# Revit family: Q-SYS NC-110
name_source: partatom
category: Communication Devices
revit_build: Autodesk Revit 2018 (Build: 20190510_1515(x64)
units: mm (PartAtom-declared; Revit-internal decimal feet)

## family parameters
Cut with Voids When Loaded = No
Host = Face
Maintain Annotation Orientation = No
Part Type = Normal
Room Calculation Point = No
Round Connector Dimension = Use Diameter
Shared = No

## types (4) — shared parameters
Camera Material = Dark Material
Camera Type = Q-SYS ePTZ with Max H FOV 110°
Current Draw = 0.021
Default Elevation = 1270 mm
Depth = 42 mm  [stored 0.137795 ft]
Description = Q-SYS Networked Fixed-Lens ePTZ Camera
Focal Length = 1.86mm
Height = 34 mm
Lens Type = Integrated, Fixed
Lens Zoom Max = 8
Manufacturer = QSC, LLC
Manufacturer URL = www.qsc.com
Model = NC-110
Motorized Zoom = No
Mount Material = Dark Material
Product Documentation Link = https://www.qsc.com
Product Page URL = https://www.qsc.com
URL = https://www.qsc.com
Voltage DC = PoE Type 1, Class 2
Weight Product (kg) = 0.4
Weight Product (lb) = 0.9
Width = 194 mm  [stored 0.636483 ft]

## per-type parameters (varying)
| type | Calc Mount Angle 1 at Base | Calc Mount Angle 2 at Camera | Mount Angle 1 at Base | Mount Angle 2 at Camera |
| Table | -45.00° | 225.00° | 135.00° | -135.00° |
| Wall Above-Display | -45.00° | 135.00° | 135.00° | -45.00° |
| Ceiling | -35.00° | 55.00° | 125.00° | 35.00° |
| Wall Below-Display | 45.00° | 45.00° | 45.00° | 45.00° |

note: [stored X ft] marks values corroborated as IEEE doubles in the binary element streams (Revit-internal decimal feet)

## geometry (parser evidence)
native form markers: Sweep x9
no freeform markers — native parametric forms only
